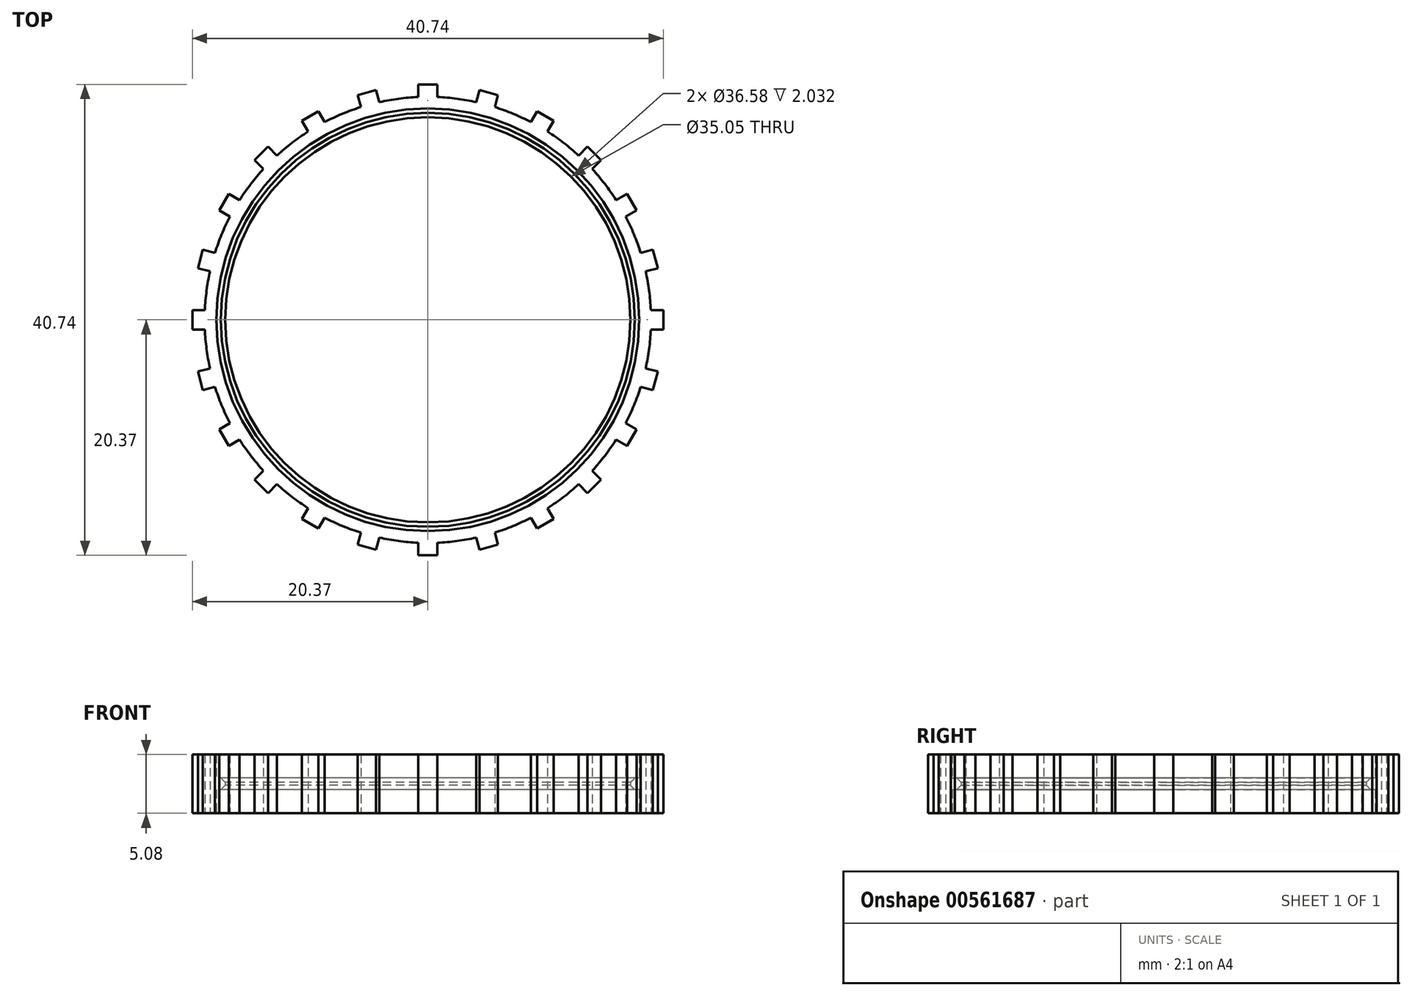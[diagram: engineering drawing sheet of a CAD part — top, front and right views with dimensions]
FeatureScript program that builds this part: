
annotation { "Feature Type Name" : "Feature", "Feature Type Description" : "" }
export const myFeature = defineFeature(function(context is Context, id is Id, definition is map)
    precondition{}
    {
        {
            var Q0;
            Q0=qCreatedBy(makeId("Top.planeOp"),FACE);
            var sketch = newSketch(context, id + "F0", { "sketchPlane" : qUnion([Q0])});
            skCircle(sketch, "E0", {"center": v(0, 0) * mm, "radius": 17.53 * mm});
            skCircle(sketch, "E1", {"center": v(0, 0) * mm, "radius": 18.29 * mm});
            skCircle(sketch, "E2", {"center": v(0, 0) * mm, "radius": 19.3 * mm});
            skPoint(sketch, "E3.middle", {"position": v(0, 19.3) * mm});
            skPoint(sketch, "E3.top.end.orphan", {"position": v(0.07, 12.47) * mm});
            skPoint(sketch, "E4.orphan", {"position": v(-12.07, 11.71) * mm});
            skLineSegment(sketch, "E5.2.0", {"start": v(0.19, 25.38) * mm, "end": v(12.34, 25.85) * mm});
            skLineSegment(sketch, "E5.3.0", {"start": v(0.31, 25) * mm, "end": v(12.47, 25.33) * mm});
            skLineSegment(sketch, "E5.4.0", {"start": v(0.43, 24.61) * mm, "end": v(12.6, 24.8) * mm});
            skLineSegment(sketch, "E5.5.0", {"start": v(0.55, 24.23) * mm, "end": v(12.71, 24.28) * mm});
            skLineSegment(sketch, "E5.6.0", {"start": v(0.66, 23.84) * mm, "end": v(12.83, 23.75) * mm});
            skLineSegment(sketch, "E5.7.0", {"start": v(0.77, 23.45) * mm, "end": v(12.93, 23.22) * mm});
            skLineSegment(sketch, "E5.8.0", {"start": v(0.87, 23.06) * mm, "end": v(13.03, 22.7) * mm});
            skLineSegment(sketch, "E5.9.0", {"start": v(0.97, 22.67) * mm, "end": v(13.12, 22.16) * mm});
            skLineSegment(sketch, "E5.10.0", {"start": v(1.06, 22.28) * mm, "end": v(13.2, 21.63) * mm});
            skLineSegment(sketch, "E5.11.0", {"start": v(1.15, 21.9) * mm, "end": v(13.3, 21.1) * mm});
            skPoint(sketch, "E5.center", {"position": v(-32.6, 14.45) * mm});
            skLineSegment(sketch, "E5.anchor1", {"start": v(-32.6, 14.45) * mm, "end": v(-0.07, 26.14) * mm, "construction": true});
            skLineSegment(sketch, "E5.anchor2", {"start": v(-32.6, 14.45) * mm, "end": v(1.46, 20.31) * mm, "construction": true});
            skPoint(sketch, "E6.orphan", {"position": v(-6.54, 13.54) * mm});
            skPoint(sketch, "E7.orphan", {"position": v(-6.52, 14.14) * mm});
            skPoint(sketch, "E8.orphan", {"position": v(-6.53, 13.84) * mm});
            skPoint(sketch, "E9.orphan", {"position": v(-6.52, 14.45) * mm});
            skPoint(sketch, "E10.orphan", {"position": v(-6.52, 14.75) * mm});
            skPoint(sketch, "E11.orphan", {"position": v(-6.53, 15.05) * mm});
            skLineSegment(sketch, "E12", {"start": v(-20.37, 0) * mm, "end": v(-20.37, 0.83) * mm});
            skLineSegment(sketch, "E13", {"start": v(-20.37, 0.83) * mm, "end": v(-19.29, 0.83) * mm});
            skLineSegment(sketch, "E14.MirrorCS", {"start": v(-20.37, 0) * mm, "end": v(-20.37, -0.83) * mm});
            skLineSegment(sketch, "E15.MirrorCS", {"start": v(-20.37, -0.83) * mm, "end": v(-19.29, -0.83) * mm});
            skPoint(sketch, "E16.start.orphan", {"position": v(-19.3, 0) * mm});
            skLineSegment(sketch, "E17.1.0", {"start": v(-19.46, -6.07) * mm, "end": v(-18.42, -5.8) * mm});
            skLineSegment(sketch, "E17.1.1", {"start": v(-19.67, -5.27) * mm, "end": v(-19.46, -6.07) * mm});
            skLineSegment(sketch, "E17.1.2", {"start": v(-19.67, -5.27) * mm, "end": v(-19.89, -4.47) * mm});
            skLineSegment(sketch, "E17.1.3", {"start": v(-19.89, -4.47) * mm, "end": v(-18.84, -4.2) * mm});
            skLineSegment(sketch, "E17.2.0", {"start": v(-17.22, -10.9) * mm, "end": v(-16.29, -10.36) * mm});
            skLineSegment(sketch, "E17.2.1", {"start": v(-17.64, -10.18) * mm, "end": v(-17.22, -10.9) * mm});
            skLineSegment(sketch, "E17.2.2", {"start": v(-17.64, -10.18) * mm, "end": v(-18.05, -9.47) * mm});
            skLineSegment(sketch, "E17.2.3", {"start": v(-18.05, -9.47) * mm, "end": v(-17.12, -8.93) * mm});
            skLineSegment(sketch, "E17.3.0", {"start": v(-13.82, -14.99) * mm, "end": v(-13.05, -14.22) * mm});
            skLineSegment(sketch, "E17.3.1", {"start": v(-14.4, -14.4) * mm, "end": v(-13.82, -14.99) * mm});
            skLineSegment(sketch, "E17.3.2", {"start": v(-14.4, -14.4) * mm, "end": v(-14.99, -13.82) * mm});
            skLineSegment(sketch, "E17.3.3", {"start": v(-14.99, -13.82) * mm, "end": v(-14.22, -13.05) * mm});
            skLineSegment(sketch, "E17.4.0", {"start": v(-9.47, -18.05) * mm, "end": v(-8.93, -17.12) * mm});
            skLineSegment(sketch, "E17.4.1", {"start": v(-10.18, -17.64) * mm, "end": v(-9.47, -18.05) * mm});
            skLineSegment(sketch, "E17.4.2", {"start": v(-10.18, -17.64) * mm, "end": v(-10.9, -17.22) * mm});
            skLineSegment(sketch, "E17.4.3", {"start": v(-10.9, -17.22) * mm, "end": v(-10.36, -16.29) * mm});
            skLineSegment(sketch, "E17.5.0", {"start": v(-4.47, -19.89) * mm, "end": v(-4.2, -18.84) * mm});
            skLineSegment(sketch, "E17.5.1", {"start": v(-5.27, -19.67) * mm, "end": v(-4.47, -19.89) * mm});
            skLineSegment(sketch, "E17.5.2", {"start": v(-5.27, -19.67) * mm, "end": v(-6.07, -19.46) * mm});
            skLineSegment(sketch, "E17.5.3", {"start": v(-6.07, -19.46) * mm, "end": v(-5.8, -18.42) * mm});
            skLineSegment(sketch, "E17.6.0", {"start": v(0.83, -20.37) * mm, "end": v(0.83, -19.29) * mm});
            skLineSegment(sketch, "E17.6.1", {"start": v(0, -20.37) * mm, "end": v(0.83, -20.37) * mm});
            skLineSegment(sketch, "E17.6.2", {"start": v(0, -20.37) * mm, "end": v(-0.83, -20.37) * mm});
            skLineSegment(sketch, "E17.6.3", {"start": v(-0.83, -20.37) * mm, "end": v(-0.83, -19.29) * mm});
            skLineSegment(sketch, "E17.7.0", {"start": v(6.07, -19.46) * mm, "end": v(5.8, -18.42) * mm});
            skLineSegment(sketch, "E17.7.1", {"start": v(5.27, -19.67) * mm, "end": v(6.07, -19.46) * mm});
            skLineSegment(sketch, "E17.7.2", {"start": v(5.27, -19.67) * mm, "end": v(4.47, -19.89) * mm});
            skLineSegment(sketch, "E17.7.3", {"start": v(4.47, -19.89) * mm, "end": v(4.2, -18.84) * mm});
            skLineSegment(sketch, "E17.8.0", {"start": v(10.9, -17.22) * mm, "end": v(10.36, -16.29) * mm});
            skLineSegment(sketch, "E17.8.1", {"start": v(10.18, -17.64) * mm, "end": v(10.9, -17.22) * mm});
            skLineSegment(sketch, "E17.8.2", {"start": v(10.18, -17.64) * mm, "end": v(9.47, -18.05) * mm});
            skLineSegment(sketch, "E17.8.3", {"start": v(9.47, -18.05) * mm, "end": v(8.93, -17.12) * mm});
            skLineSegment(sketch, "E17.9.0", {"start": v(14.99, -13.82) * mm, "end": v(14.22, -13.05) * mm});
            skLineSegment(sketch, "E17.9.1", {"start": v(14.4, -14.4) * mm, "end": v(14.99, -13.82) * mm});
            skLineSegment(sketch, "E17.9.2", {"start": v(14.4, -14.4) * mm, "end": v(13.82, -14.99) * mm});
            skLineSegment(sketch, "E17.9.3", {"start": v(13.82, -14.99) * mm, "end": v(13.05, -14.22) * mm});
            skLineSegment(sketch, "E17.10.0", {"start": v(18.05, -9.47) * mm, "end": v(17.12, -8.93) * mm});
            skLineSegment(sketch, "E17.10.1", {"start": v(17.64, -10.18) * mm, "end": v(18.05, -9.47) * mm});
            skLineSegment(sketch, "E17.10.2", {"start": v(17.64, -10.18) * mm, "end": v(17.22, -10.9) * mm});
            skLineSegment(sketch, "E17.10.3", {"start": v(17.22, -10.9) * mm, "end": v(16.29, -10.36) * mm});
            skLineSegment(sketch, "E17.11.0", {"start": v(19.89, -4.47) * mm, "end": v(18.84, -4.2) * mm});
            skLineSegment(sketch, "E17.11.1", {"start": v(19.67, -5.27) * mm, "end": v(19.89, -4.47) * mm});
            skLineSegment(sketch, "E17.11.2", {"start": v(19.67, -5.27) * mm, "end": v(19.46, -6.07) * mm});
            skLineSegment(sketch, "E17.11.3", {"start": v(19.46, -6.07) * mm, "end": v(18.42, -5.8) * mm});
            skLineSegment(sketch, "E17.12.0", {"start": v(20.37, 0.83) * mm, "end": v(19.29, 0.83) * mm});
            skLineSegment(sketch, "E17.12.1", {"start": v(20.37, 0) * mm, "end": v(20.37, 0.83) * mm});
            skLineSegment(sketch, "E17.12.2", {"start": v(20.37, 0) * mm, "end": v(20.37, -0.83) * mm});
            skLineSegment(sketch, "E17.12.3", {"start": v(20.37, -0.83) * mm, "end": v(19.29, -0.83) * mm});
            skLineSegment(sketch, "E17.13.0", {"start": v(19.46, 6.07) * mm, "end": v(18.42, 5.8) * mm});
            skLineSegment(sketch, "E17.13.1", {"start": v(19.67, 5.27) * mm, "end": v(19.46, 6.07) * mm});
            skLineSegment(sketch, "E17.13.2", {"start": v(19.67, 5.27) * mm, "end": v(19.89, 4.47) * mm});
            skLineSegment(sketch, "E17.13.3", {"start": v(19.89, 4.47) * mm, "end": v(18.84, 4.2) * mm});
            skLineSegment(sketch, "E18.1.14.0", {"start": v(17.22, 10.9) * mm, "end": v(16.29, 10.36) * mm});
            skLineSegment(sketch, "E18.3.14.0", {"start": v(17.64, 10.18) * mm, "end": v(17.22, 10.9) * mm});
            skLineSegment(sketch, "E18.6.14.0", {"start": v(17.64, 10.18) * mm, "end": v(18.05, 9.47) * mm});
            skLineSegment(sketch, "E18.9.14.0", {"start": v(18.05, 9.47) * mm, "end": v(17.12, 8.93) * mm});
            skLineSegment(sketch, "E18.1.15.0", {"start": v(13.82, 14.99) * mm, "end": v(13.05, 14.22) * mm});
            skLineSegment(sketch, "E18.3.15.0", {"start": v(14.4, 14.4) * mm, "end": v(13.82, 14.99) * mm});
            skLineSegment(sketch, "E18.6.15.0", {"start": v(14.4, 14.4) * mm, "end": v(14.99, 13.82) * mm});
            skLineSegment(sketch, "E18.9.15.0", {"start": v(14.99, 13.82) * mm, "end": v(14.22, 13.05) * mm});
            skLineSegment(sketch, "E19.1.16.0", {"start": v(9.47, 18.05) * mm, "end": v(8.93, 17.12) * mm});
            skLineSegment(sketch, "E19.3.16.0", {"start": v(10.18, 17.64) * mm, "end": v(9.47, 18.05) * mm});
            skLineSegment(sketch, "E19.6.16.0", {"start": v(10.18, 17.64) * mm, "end": v(10.9, 17.22) * mm});
            skLineSegment(sketch, "E19.9.16.0", {"start": v(10.9, 17.22) * mm, "end": v(10.36, 16.29) * mm});
            skLineSegment(sketch, "E19.1.17.0", {"start": v(4.47, 19.89) * mm, "end": v(4.2, 18.84) * mm});
            skLineSegment(sketch, "E19.3.17.0", {"start": v(5.27, 19.67) * mm, "end": v(4.47, 19.89) * mm});
            skLineSegment(sketch, "E19.6.17.0", {"start": v(5.27, 19.67) * mm, "end": v(6.07, 19.46) * mm});
            skLineSegment(sketch, "E19.9.17.0", {"start": v(6.07, 19.46) * mm, "end": v(5.8, 18.42) * mm});
            skLineSegment(sketch, "E19.1.18.0", {"start": v(-0.83, 20.37) * mm, "end": v(-0.83, 19.29) * mm});
            skLineSegment(sketch, "E19.3.18.0", {"start": v(0, 20.37) * mm, "end": v(-0.83, 20.37) * mm});
            skLineSegment(sketch, "E19.6.18.0", {"start": v(0, 20.37) * mm, "end": v(0.83, 20.37) * mm});
            skLineSegment(sketch, "E19.9.18.0", {"start": v(0.83, 20.37) * mm, "end": v(0.83, 19.29) * mm});
            skLineSegment(sketch, "E19.1.19.0", {"start": v(-6.07, 19.46) * mm, "end": v(-5.8, 18.42) * mm});
            skLineSegment(sketch, "E19.3.19.0", {"start": v(-5.27, 19.67) * mm, "end": v(-6.07, 19.46) * mm});
            skLineSegment(sketch, "E19.6.19.0", {"start": v(-5.27, 19.67) * mm, "end": v(-4.47, 19.89) * mm});
            skLineSegment(sketch, "E19.9.19.0", {"start": v(-4.47, 19.89) * mm, "end": v(-4.2, 18.84) * mm});
            skLineSegment(sketch, "E19.1.20.0", {"start": v(-10.9, 17.22) * mm, "end": v(-10.36, 16.29) * mm});
            skLineSegment(sketch, "E19.3.20.0", {"start": v(-10.18, 17.64) * mm, "end": v(-10.9, 17.22) * mm});
            skLineSegment(sketch, "E19.6.20.0", {"start": v(-10.18, 17.64) * mm, "end": v(-9.47, 18.05) * mm});
            skLineSegment(sketch, "E19.9.20.0", {"start": v(-9.47, 18.05) * mm, "end": v(-8.93, 17.12) * mm});
            skLineSegment(sketch, "E19.1.21.0", {"start": v(-14.99, 13.82) * mm, "end": v(-14.22, 13.05) * mm});
            skLineSegment(sketch, "E19.3.21.0", {"start": v(-14.4, 14.4) * mm, "end": v(-14.99, 13.82) * mm});
            skLineSegment(sketch, "E19.6.21.0", {"start": v(-14.4, 14.4) * mm, "end": v(-13.82, 14.99) * mm});
            skLineSegment(sketch, "E19.9.21.0", {"start": v(-13.82, 14.99) * mm, "end": v(-13.05, 14.22) * mm});
            skLineSegment(sketch, "E19.1.22.0", {"start": v(-18.05, 9.47) * mm, "end": v(-17.12, 8.93) * mm});
            skLineSegment(sketch, "E19.3.22.0", {"start": v(-17.64, 10.18) * mm, "end": v(-18.05, 9.47) * mm});
            skLineSegment(sketch, "E19.6.22.0", {"start": v(-17.64, 10.18) * mm, "end": v(-17.22, 10.9) * mm});
            skLineSegment(sketch, "E19.9.22.0", {"start": v(-17.22, 10.9) * mm, "end": v(-16.29, 10.36) * mm});
            skLineSegment(sketch, "E19.1.23.0", {"start": v(-19.89, 4.47) * mm, "end": v(-18.84, 4.2) * mm});
            skLineSegment(sketch, "E19.3.23.0", {"start": v(-19.67, 5.27) * mm, "end": v(-19.89, 4.47) * mm});
            skLineSegment(sketch, "E19.6.23.0", {"start": v(-19.67, 5.27) * mm, "end": v(-19.46, 6.07) * mm});
            skLineSegment(sketch, "E19.9.23.0", {"start": v(-19.46, 6.07) * mm, "end": v(-18.42, 5.8) * mm});
            skSolve(sketch);
        }
        {
            var Q0;
            Q0=makeQuery(id+"F0.imprint","IMPRINT",FACE,{"disambiguationData":[TD([[makeQuery(id+"F0.imprint","IMPRINT",EDGE,{"derivedFrom":sQuery(id+"F0.wireOp",EDGE,"E1")}),-1.0]])]});
            var Q1;
            Q1=makeQuery(id+"F0.imprint","IMPRINT",FACE,{"disambiguationData":[TD([[makeQuery(id+"F0.imprint","IMPRINT",EDGE,{"derivedFrom":sQuery(id+"F0.wireOp",EDGE,"8cd5e674-b474-4cb0-8a18-ed70cfcb54b6.1.14.0")}),-1.0]])]});
            var Q2;
            Q2=makeQuery(id+"F0.imprint","IMPRINT",FACE,{"disambiguationData":[TD([[makeQuery(id+"F0.imprint","IMPRINT",EDGE,{"derivedFrom":sQuery(id+"F0.wireOp",EDGE,"8cd5e674-b474-4cb0-8a18-ed70cfcb54b6.1.15.0")}),-1.0]])]});
            var Q3;
            Q3=makeQuery(id+"F0.imprint","IMPRINT",FACE,{"disambiguationData":[TD([[makeQuery(id+"F0.imprint","IMPRINT",EDGE,{"derivedFrom":sQuery(id+"F0.wireOp",EDGE,"E3.bottom")}),-1.0]])]});
            var Q4;
            Q4=makeQuery(id+"F0.imprint","IMPRINT",FACE,{"disambiguationData":[TD([[makeQuery(id+"F0.imprint","IMPRINT",EDGE,{"derivedFrom":sQuery(id+"F0.wireOp",EDGE,"E5.1.0")}),-1.0]])]});
            var Q5;
            Q5=makeQuery(id+"F0.imprint","IMPRINT",FACE,{"disambiguationData":[TD([[makeQuery(id+"F0.imprint","IMPRINT",EDGE,{"derivedFrom":sQuery(id+"F0.wireOp",EDGE,"8cd5e674-b474-4cb0-8a18-ed70cfcb54b6.1.13.0")}),-1.0]])]});
            var Q6;
            Q6=makeQuery(id+"F0.imprint","IMPRINT",FACE,{"disambiguationData":[TD([[makeQuery(id+"F0.imprint","IMPRINT",EDGE,{"derivedFrom":sQuery(id+"F0.wireOp",EDGE,"E5.2.0")}),-1.0]])]});
            var Q7;
            Q7=makeQuery(id+"F0.imprint","IMPRINT",FACE,{"disambiguationData":[TD([[makeQuery(id+"F0.imprint","IMPRINT",EDGE,{"derivedFrom":sQuery(id+"F0.wireOp",EDGE,"E5.3.0")}),-1.0]])]});
            var Q8;
            Q8=makeQuery(id+"F0.imprint","IMPRINT",FACE,{"disambiguationData":[TD([[makeQuery(id+"F0.imprint","IMPRINT",EDGE,{"derivedFrom":sQuery(id+"F0.wireOp",EDGE,"E5.4.0")}),-1.0]])]});
            var Q9;
            Q9=makeQuery(id+"F0.imprint","IMPRINT",FACE,{"disambiguationData":[TD([[makeQuery(id+"F0.imprint","IMPRINT",EDGE,{"derivedFrom":sQuery(id+"F0.wireOp",EDGE,"E5.5.0")}),-1.0]])]});
            var Q10;
            Q10=makeQuery(id+"F0.imprint","IMPRINT",FACE,{"disambiguationData":[TD([[makeQuery(id+"F0.imprint","IMPRINT",EDGE,{"derivedFrom":sQuery(id+"F0.wireOp",EDGE,"E5.6.0")}),-1.0]])]});
            var Q11;
            Q11=makeQuery(id+"F0.imprint","IMPRINT",FACE,{"disambiguationData":[TD([[makeQuery(id+"F0.imprint","IMPRINT",EDGE,{"derivedFrom":sQuery(id+"F0.wireOp",EDGE,"E5.7.0")}),-1.0]])]});
            var Q12;
            Q12=makeQuery(id+"F0.imprint","IMPRINT",FACE,{"disambiguationData":[TD([[makeQuery(id+"F0.imprint","IMPRINT",EDGE,{"derivedFrom":sQuery(id+"F0.wireOp",EDGE,"E5.8.0")}),-1.0]])]});
            var Q13;
            Q13=makeQuery(id+"F0.imprint","IMPRINT",FACE,{"disambiguationData":[TD([[makeQuery(id+"F0.imprint","IMPRINT",EDGE,{"derivedFrom":sQuery(id+"F0.wireOp",EDGE,"E5.9.0")}),-1.0]])]});
            var Q14;
            Q14=makeQuery(id+"F0.imprint","IMPRINT",FACE,{"disambiguationData":[TD([[makeQuery(id+"F0.imprint","IMPRINT",EDGE,{"derivedFrom":sQuery(id+"F0.wireOp",EDGE,"8cd5e674-b474-4cb0-8a18-ed70cfcb54b6.1.12.0")}),-1.0]])]});
            var Q15;
            Q15=makeQuery(id+"F0.imprint","IMPRINT",FACE,{"disambiguationData":[TD([[makeQuery(id+"F0.imprint","IMPRINT",EDGE,{"derivedFrom":sQuery(id+"F0.wireOp",EDGE,"E5.11.0")}),-1.0]])]});
            var Q16;
            Q16=makeQuery(id+"F0.imprint","IMPRINT",FACE,{"disambiguationData":[TD([[makeQuery(id+"F0.imprint","IMPRINT",EDGE,{"derivedFrom":sQuery(id+"F0.wireOp",EDGE,"E5.10.0")}),-1.0]])]});
            var Q17;
            {var subQ0=sQuery(id+"F0.wireOp",EDGE,"E18.1.14.0");Q17=makeQuery(id+"F0.imprint","IMPRINT",FACE,{"disambiguationData":[TD([[makeQuery(id+"F0.imprint","IMPRINT",EDGE,{"derivedFrom":subQ0}),1.0]])]});}
            var Q18;
            {var subQ0=sQuery(id+"F0.wireOp",EDGE,"E18.1.15.0");Q18=makeQuery(id+"F0.imprint","IMPRINT",FACE,{"disambiguationData":[TD([[makeQuery(id+"F0.imprint","IMPRINT",EDGE,{"derivedFrom":subQ0}),1.0]])]});}
            var Q19;
            {var subQ0=sQuery(id+"F0.wireOp",EDGE,"E17.13.0");Q19=makeQuery(id+"F0.imprint","IMPRINT",FACE,{"disambiguationData":[TD([[makeQuery(id+"F0.imprint","IMPRINT",EDGE,{"derivedFrom":subQ0}),1.0]])]});}
            var Q20;
            {var subQ0=sQuery(id+"F0.wireOp",EDGE,"E17.12.0");Q20=makeQuery(id+"F0.imprint","IMPRINT",FACE,{"disambiguationData":[TD([[makeQuery(id+"F0.imprint","IMPRINT",EDGE,{"derivedFrom":subQ0}),1.0]])]});}
            var Q21;
            {var subQ0=sQuery(id+"F0.wireOp",EDGE,"E17.11.0");Q21=makeQuery(id+"F0.imprint","IMPRINT",FACE,{"disambiguationData":[TD([[makeQuery(id+"F0.imprint","IMPRINT",EDGE,{"derivedFrom":subQ0}),1.0]])]});}
            var Q22;
            {var subQ0=sQuery(id+"F0.wireOp",EDGE,"E17.10.0");Q22=makeQuery(id+"F0.imprint","IMPRINT",FACE,{"disambiguationData":[TD([[makeQuery(id+"F0.imprint","IMPRINT",EDGE,{"derivedFrom":subQ0}),1.0]])]});}
            var Q23;
            {var subQ0=sQuery(id+"F0.wireOp",EDGE,"E17.9.0");Q23=makeQuery(id+"F0.imprint","IMPRINT",FACE,{"disambiguationData":[TD([[makeQuery(id+"F0.imprint","IMPRINT",EDGE,{"derivedFrom":subQ0}),1.0]])]});}
            var Q24;
            Q24=makeQuery(id+"F0.imprint","IMPRINT",FACE,{"disambiguationData":[TD([[makeQuery(id+"F0.imprint","IMPRINT",EDGE,{"derivedFrom":sQuery(id+"F0.wireOp",EDGE,"E12")}),-1.0]])]});
            var Q25;
            {var subQ0=sQuery(id+"F0.wireOp",EDGE,"E17.1.0");Q25=makeQuery(id+"F0.imprint","IMPRINT",FACE,{"disambiguationData":[TD([[makeQuery(id+"F0.imprint","IMPRINT",EDGE,{"derivedFrom":subQ0}),1.0]])]});}
            var Q26;
            {var subQ0=sQuery(id+"F0.wireOp",EDGE,"E17.2.0");Q26=makeQuery(id+"F0.imprint","IMPRINT",FACE,{"disambiguationData":[TD([[makeQuery(id+"F0.imprint","IMPRINT",EDGE,{"derivedFrom":subQ0}),1.0]])]});}
            var Q27;
            {var subQ0=sQuery(id+"F0.wireOp",EDGE,"E17.3.0");Q27=makeQuery(id+"F0.imprint","IMPRINT",FACE,{"disambiguationData":[TD([[makeQuery(id+"F0.imprint","IMPRINT",EDGE,{"derivedFrom":subQ0}),1.0]])]});}
            var Q28;
            {var subQ0=sQuery(id+"F0.wireOp",EDGE,"E17.4.0");Q28=makeQuery(id+"F0.imprint","IMPRINT",FACE,{"disambiguationData":[TD([[makeQuery(id+"F0.imprint","IMPRINT",EDGE,{"derivedFrom":subQ0}),1.0]])]});}
            var Q29;
            {var subQ0=sQuery(id+"F0.wireOp",EDGE,"E17.5.0");Q29=makeQuery(id+"F0.imprint","IMPRINT",FACE,{"disambiguationData":[TD([[makeQuery(id+"F0.imprint","IMPRINT",EDGE,{"derivedFrom":subQ0}),1.0]])]});}
            var Q30;
            {var subQ0=sQuery(id+"F0.wireOp",EDGE,"E17.6.0");Q30=makeQuery(id+"F0.imprint","IMPRINT",FACE,{"disambiguationData":[TD([[makeQuery(id+"F0.imprint","IMPRINT",EDGE,{"derivedFrom":subQ0}),1.0]])]});}
            var Q31;
            {var subQ0=sQuery(id+"F0.wireOp",EDGE,"E17.7.0");Q31=makeQuery(id+"F0.imprint","IMPRINT",FACE,{"disambiguationData":[TD([[makeQuery(id+"F0.imprint","IMPRINT",EDGE,{"derivedFrom":subQ0}),1.0]])]});}
            var Q32;
            {var subQ0=sQuery(id+"F0.wireOp",EDGE,"E17.8.0");Q32=makeQuery(id+"F0.imprint","IMPRINT",FACE,{"disambiguationData":[TD([[makeQuery(id+"F0.imprint","IMPRINT",EDGE,{"derivedFrom":subQ0}),1.0]])]});}
            extrude(context, id + "F1", {"entities" : qUnion([Q0, Q1, Q2, Q3, Q4, Q5, Q6, Q7, Q8, Q9, Q10, Q11, Q12, Q13, Q14, Q15, Q16, Q17, Q18, Q19, Q20, Q21, Q22, Q23, Q24, Q25, Q26, Q27, Q28, Q29, Q30, Q31, Q32]), "endBound" : BoundingType.SYMMETRIC, "depth" : 5.08 * mm, "offsetDistance" : 25.4 * mm});
        }
        {
            var Q0;
            Q0=makeQuery(id+"F0.imprint","IMPRINT",FACE,{"disambiguationData":[TD([[makeQuery(id+"F0.imprint","IMPRINT",EDGE,{"derivedFrom":sQuery(id+"F0.wireOp",EDGE,"E0")}),-1.0]])]});
            extrude(context, id + "F2", {"entities" : qUnion([Q0]), "operationType" : NewBodyOperationType.ADD, "endBound" : BoundingType.SYMMETRIC, "depth" : 1.02 * mm, "offsetDistance" : 25.4 * mm});
        }
        {
            var Q0;
            Q0=makeQuery(id+"F2.opExtrude","SWEPT_FACE",FACE,{"disambiguationData":[OSD([sQuery(id+"F0.wireOp",EDGE,"E0")])]});
            chamfer(context, id + "F3", {"entities" : qUnion([Q0]), "width" : 0.38 * mm, "tangentPropagation" : true});
        }
        {
            var Q0;
            {var subQ0=sQuery(id+"F0.wireOp",EDGE,"E19.1.16.0");Q0=makeQuery(id+"F0.imprint","IMPRINT",FACE,{"disambiguationData":[TD([[makeQuery(id+"F0.imprint","IMPRINT",EDGE,{"derivedFrom":subQ0}),1.0]])]});}
            var Q1;
            {var subQ0=sQuery(id+"F0.wireOp",EDGE,"E19.1.17.0");Q1=makeQuery(id+"F0.imprint","IMPRINT",FACE,{"disambiguationData":[TD([[makeQuery(id+"F0.imprint","IMPRINT",EDGE,{"derivedFrom":subQ0}),1.0]])]});}
            var Q2;
            {var subQ0=sQuery(id+"F0.wireOp",EDGE,"E19.1.18.0");Q2=makeQuery(id+"F0.imprint","IMPRINT",FACE,{"disambiguationData":[TD([[makeQuery(id+"F0.imprint","IMPRINT",EDGE,{"derivedFrom":subQ0}),1.0]])]});}
            var Q3;
            {var subQ0=sQuery(id+"F0.wireOp",EDGE,"E19.1.19.0");Q3=makeQuery(id+"F0.imprint","IMPRINT",FACE,{"disambiguationData":[TD([[makeQuery(id+"F0.imprint","IMPRINT",EDGE,{"derivedFrom":subQ0}),1.0]])]});}
            var Q4;
            {var subQ0=sQuery(id+"F0.wireOp",EDGE,"E19.1.20.0");Q4=makeQuery(id+"F0.imprint","IMPRINT",FACE,{"disambiguationData":[TD([[makeQuery(id+"F0.imprint","IMPRINT",EDGE,{"derivedFrom":subQ0}),1.0]])]});}
            var Q5;
            {var subQ0=sQuery(id+"F0.wireOp",EDGE,"E19.1.21.0");Q5=makeQuery(id+"F0.imprint","IMPRINT",FACE,{"disambiguationData":[TD([[makeQuery(id+"F0.imprint","IMPRINT",EDGE,{"derivedFrom":subQ0}),1.0]])]});}
            var Q6;
            {var subQ0=sQuery(id+"F0.wireOp",EDGE,"E19.1.22.0");Q6=makeQuery(id+"F0.imprint","IMPRINT",FACE,{"disambiguationData":[TD([[makeQuery(id+"F0.imprint","IMPRINT",EDGE,{"derivedFrom":subQ0}),1.0]])]});}
            var Q7;
            {var subQ0=sQuery(id+"F0.wireOp",EDGE,"E19.1.23.0");Q7=makeQuery(id+"F0.imprint","IMPRINT",FACE,{"disambiguationData":[TD([[makeQuery(id+"F0.imprint","IMPRINT",EDGE,{"derivedFrom":subQ0}),1.0]])]});}
            extrude(context, id + "F4", {"entities" : qUnion([Q0, Q1, Q2, Q3, Q4, Q5, Q6, Q7]), "operationType" : NewBodyOperationType.ADD, "endBound" : BoundingType.SYMMETRIC, "depth" : 5.08 * mm, "offsetDistance" : 25.4 * mm});
        }
    });
